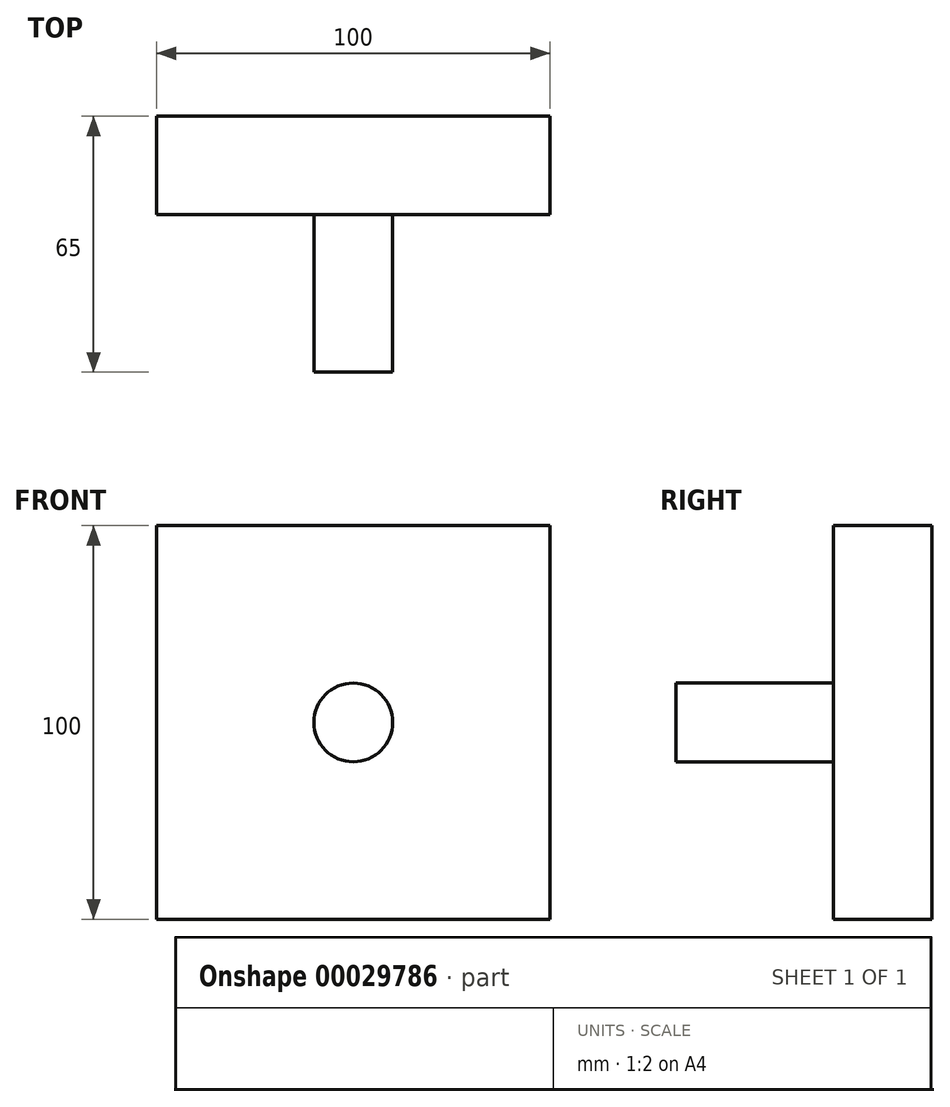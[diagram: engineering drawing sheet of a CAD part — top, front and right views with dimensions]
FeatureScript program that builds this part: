
annotation { "Feature Type Name" : "Feature", "Feature Type Description" : "" }
export const myFeature = defineFeature(function(context is Context, id is Id, definition is map)
    precondition{}
    {
        {
            var Q0;
            Q0=qCreatedBy(makeId("Front.planeOp"),FACE);
            var sketch = newSketch(context, id + "F0", { "sketchPlane" : qUnion([Q0])});
            skLineSegment(sketch, "E0.bottom", {"start": v(0, 0) * mm, "end": v(100, 0) * mm});
            skLineSegment(sketch, "E0.top", {"start": v(0, 100) * mm, "end": v(100, 100) * mm});
            skLineSegment(sketch, "E0.left", {"start": v(0, 0) * mm, "end": v(0, 100) * mm});
            skLineSegment(sketch, "E0.right", {"start": v(100, 0) * mm, "end": v(100, 100) * mm});
            skSolve(sketch);
        }
        {
            var Q0;
            Q0 = qSketchRegion(id + "F0", true);
            extrude(context, id + "F1", {"entities" : qUnion([Q0]), "depth" : 25 * mm});
        }
        {
            var Q0;
            Q0=makeQuery(id+"F1.opExtrude","CAP_FACE",FACE,{"disambiguationData":[OSD([sQuery(id+"F0.wireOp",EDGE,"E0.bottom"),sQuery(id+"F0.wireOp",EDGE,"E0.top"),sQuery(id+"F0.wireOp",EDGE,"E0.left"),sQuery(id+"F0.wireOp",EDGE,"E0.right")])],"isStart":false});
            var sketch = newSketch(context, id + "F2", { "sketchPlane" : qUnion([Q0])});
            skCircle(sketch, "E1", {"center": v(50, 50) * mm, "radius": 10 * mm});
            skSolve(sketch);
        }
        {
            var Q0;
            Q0 = qSketchRegion(id + "F2", true);
            extrude(context, id + "F3", {"entities" : qUnion([Q0]), "operationType" : NewBodyOperationType.ADD, "depth" : 40 * mm});
        }
    });
